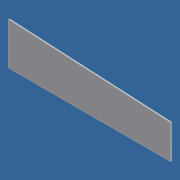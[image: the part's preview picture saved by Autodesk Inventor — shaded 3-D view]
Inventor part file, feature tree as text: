
AUTODESK INVENTOR PART (.ipt)
format: ipt  version: 2012 (Build 160160000, 160)  size: 64,512 bytes
history: native  units: in
note: dims shown in document units (in); Inventor stores cm internally (conversion verified against a paired STEP export)
features: extrude x1, sketch x1
ambient origin geometry x8: Origin, YZ Plane, XZ Plane, XY Plane, X Axis, Y Axis, Z Axis, Center Point
bodies: Solid1 (feature_tree)
feature tree (2):
  extrude  "Extrusion1"  Depth=10.0in
  sketch  "Sketch1"  dims[d0=8.0in d1=10.0in d2=38.5in d3=0.25in d4=0.0in]
